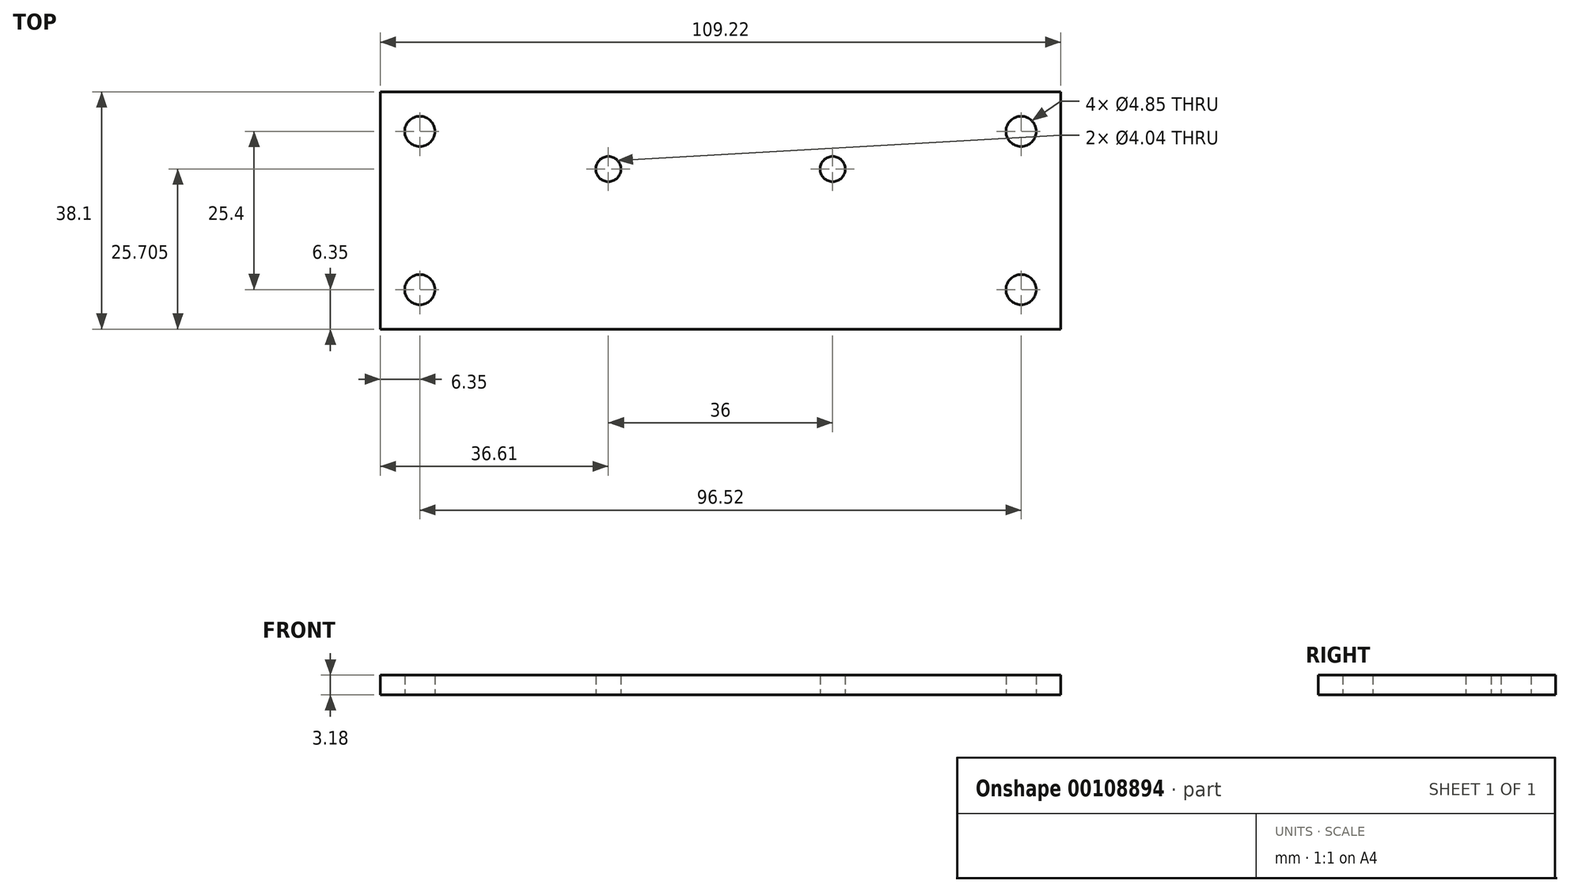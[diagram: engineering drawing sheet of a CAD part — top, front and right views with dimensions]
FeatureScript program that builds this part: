
annotation { "Feature Type Name" : "Feature", "Feature Type Description" : "" }
export const myFeature = defineFeature(function(context is Context, id is Id, definition is map)
    precondition{}
    {
        {
            var Q0;
            Q0=qCreatedBy(makeId("Top.planeOp"),FACE);
            var sketch = newSketch(context, id + "F0", { "sketchPlane" : qUnion([Q0])});
            skLineSegment(sketch, "E0.bottom", {"start": v(54.61, 19.05) * mm, "end": v(-54.61, 19.05) * mm});
            skLineSegment(sketch, "E0.top", {"start": v(54.61, -19.05) * mm, "end": v(-54.61, -19.05) * mm});
            skLineSegment(sketch, "E0.left", {"start": v(54.61, 19.05) * mm, "end": v(54.61, -19.05) * mm});
            skLineSegment(sketch, "E0.right", {"start": v(-54.61, 19.05) * mm, "end": v(-54.61, -19.05) * mm});
            skPoint(sketch, "E0.middle", {"position": v(0, 0) * mm});
            skCircle(sketch, "E1", {"center": v(-48.26, 12.7) * mm, "radius": 2.43 * mm});
            skCircle(sketch, "E2.MirrorC", {"center": v(48.26, 12.7) * mm, "radius": 2.43 * mm});
            skCircle(sketch, "E3.MirrorC", {"center": v(-48.26, -12.7) * mm, "radius": 2.43 * mm});
            skCircle(sketch, "E4.MirrorC", {"center": v(48.26, -12.7) * mm, "radius": 2.43 * mm});
            skCircle(sketch, "E5", {"center": v(-18, 6.65) * mm, "radius": 2.02 * mm});
            skCircle(sketch, "E6.MirrorC", {"center": v(18, 6.65) * mm, "radius": 2.02 * mm});
            skSolve(sketch);
        }
        {
            var Q0;
            Q0=makeQuery(id+"F0.imprint","IMPRINT",FACE,{"disambiguationData":[TD([[makeQuery(id+"F0.imprint","IMPRINT",EDGE,{"derivedFrom":sQuery(id+"F0.wireOp",EDGE,"E0.bottom")}),1.0]])]});
            extrude(context, id + "F1", {"entities" : qUnion([Q0]), "depth" : 3.17 * mm});
        }
    });
